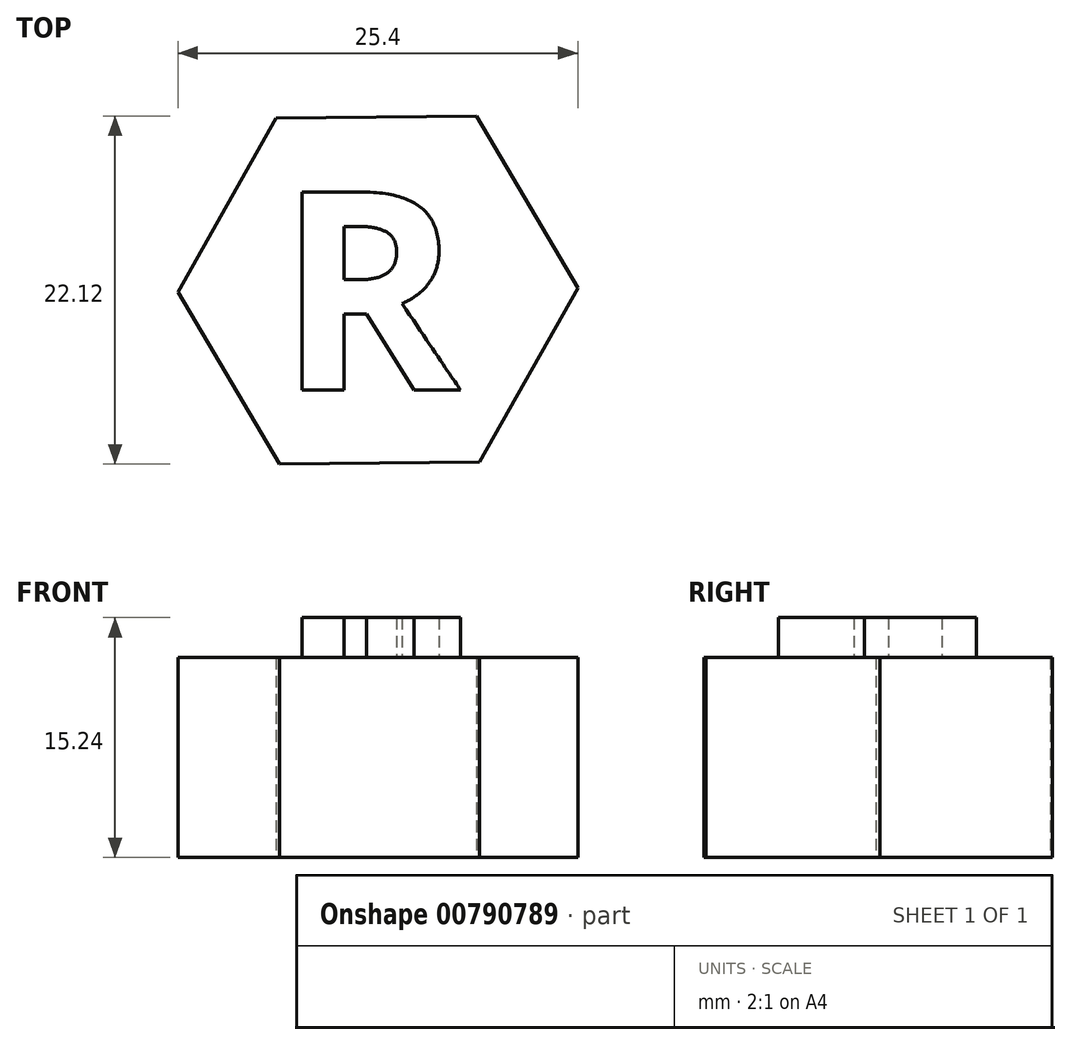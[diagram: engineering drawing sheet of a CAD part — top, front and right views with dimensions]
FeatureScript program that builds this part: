
annotation { "Feature Type Name" : "Feature", "Feature Type Description" : "" }
export const myFeature = defineFeature(function(context is Context, id is Id, definition is map)
    precondition{}
    {
        {
            var Q0;
            Q0=qCreatedBy(makeId("Top.planeOp"),FACE);
            var sketch = newSketch(context, id + "F0", { "sketchPlane" : qUnion([Q0])});
            skCircle(sketch, "E0.cCircle", {"center": v(0, 0) * mm, "radius": 11 * mm, "construction": true});
            skLineSegment(sketch, "E0.0", {"start": v(6.24, 11.06) * mm, "end": v(12.7, 0.13) * mm});
            skLineSegment(sketch, "E0.1", {"start": v(12.7, 0.13) * mm, "end": v(6.46, -10.94) * mm});
            skLineSegment(sketch, "E0.2", {"start": v(6.46, -10.94) * mm, "end": v(-6.24, -11.06) * mm});
            skLineSegment(sketch, "E0.3", {"start": v(-6.24, -11.06) * mm, "end": v(-12.7, -0.13) * mm});
            skLineSegment(sketch, "E0.4", {"start": v(-12.7, -0.13) * mm, "end": v(-6.46, 10.94) * mm});
            skLineSegment(sketch, "E0.5", {"start": v(-6.46, 10.94) * mm, "end": v(6.24, 11.06) * mm});
            skPoint(sketch, "E0.0.midPoint", {"position": v(9.47, 5.6) * mm});
            skSolve(sketch);
        }
        {
            var Q0;
            Q0=qSketchRegion(id+"F0",true);
            extrude(context, id + "F1", {"entities" : qUnion([Q0]), "depth" : 12.7 * mm, "offsetDistance" : 25.4 * mm});
        }
        {
            var Q0;
            Q0=makeQuery(id+"F1.opExtrude","CAP_FACE",FACE,{"disambiguationData":[OSD([sQuery(id+"F0.wireOp",EDGE,"E0.0"),sQuery(id+"F0.wireOp",EDGE,"E0.1"),sQuery(id+"F0.wireOp",EDGE,"E0.2"),sQuery(id+"F0.wireOp",EDGE,"E0.3"),sQuery(id+"F0.wireOp",EDGE,"E0.4"),sQuery(id+"F0.wireOp",EDGE,"E0.5")])],"isStart":false});
            var sketch = newSketch(context, id + "F2", { "sketchPlane" : qUnion([Q0])});
            skText(sketch, "E1", { "text": "R", "fontName": "OpenSans-Bold.ttf"});
            const initialGuessF2  = {"E1": [-0.00639, -0.00634, 1, 0, 0.01268]};
            skSetInitialGuess(sketch, initialGuessF2);
            skSolve(sketch);
        }
        {
            var Q0;
            Q0 = qSketchRegion(id + "F2", true);
            extrude(context, id + "F3", {"entities" : qUnion([Q0]), "operationType" : NewBodyOperationType.ADD, "depth" : 2.54 * mm, "offsetDistance" : 25.4 * mm});
        }
    });
